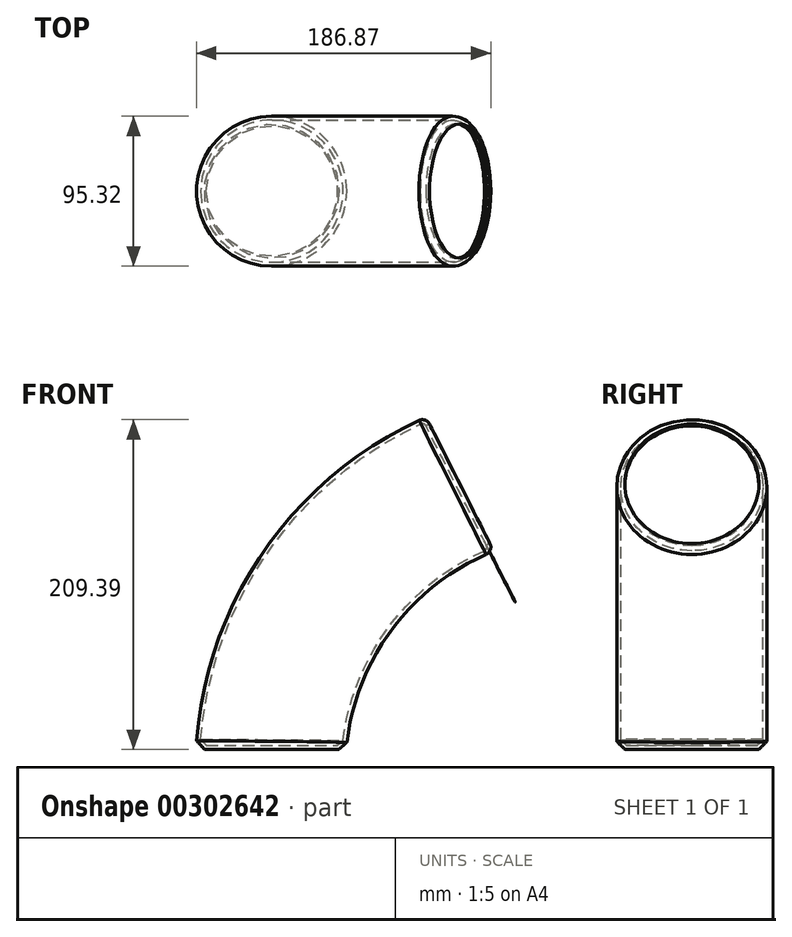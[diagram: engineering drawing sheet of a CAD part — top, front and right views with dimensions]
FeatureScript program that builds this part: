
annotation { "Feature Type Name" : "Feature", "Feature Type Description" : "" }
export const myFeature = defineFeature(function(context is Context, id is Id, definition is map)
    precondition{}
    {
        {
            var Q0;
            Q0=qCreatedBy(makeId("Top.planeOp"),FACE);
            var sketch = newSketch(context, id + "F0", { "sketchPlane" : qUnion([Q0])});
            skCircle(sketch, "E0", {"center": v(0, 0) * mm, "radius": 47.66 * mm});
            skSolve(sketch);
        }
        {
            var Q0;
            Q0=qCreatedBy(makeId("Front.planeOp"),FACE);
            var sketch = newSketch(context, id + "F1", { "sketchPlane" : qUnion([Q0])});
            skArc(sketch, "E1", {"start": v(119.97, 168.41) * mm, "mid": v(36.17, 101.17) * mm, "end": v(0, 0) * mm});
            skSolve(sketch);
        }
        {
            var Q0;
            Q0=makeQuery(id+"F0.imprint","IMPRINT",FACE,{"disambiguationData":[TD([[makeQuery(id+"F0.imprint","IMPRINT",EDGE,{"derivedFrom":sQuery(id+"F0.wireOp",EDGE,"E0")}),1.0]])]});
            var Q1;
            Q1=sQuery(id+"F1.wireOp",EDGE,"E1");
            sweep(context, id + "F2", {"profiles" : qUnion([Q0]), "path" : qUnion([Q1])});
        }
        {
            var Q0;
            Q0=makeQuery(id+"F2.opSweep","CAP_EDGE",EDGE,{"disambiguationData":[OSD([sQuery(id+"F0.wireOp",EDGE,"E0"),sQuery(id+"F1.wireOp",VERTEX,"E1.start")])],"isStart":false});
            fillet(context, id + "F3", {"entities" : qUnion([Q0]), "radius" : 5.08 * mm, "tangentPropagation" : true, "allowEdgeOverflow" : false});
        }
        {
            var Q0;
            Q0=makeQuery(id+"F2.opSweep","CAP_EDGE",EDGE,{"disambiguationData":[OSD([sQuery(id+"F0.wireOp",EDGE,"E0"),sQuery(id+"F1.wireOp",VERTEX,"E1.end")])],"isStart":true});
            chamfer(context, id + "F4", {"entities" : qUnion([Q0]), "width" : 5.08 * mm, "tangentPropagation" : true});
        }
        {
            var Q0;
            Q0=makeQuery(id+"F2.opSweep","CAP_FACE",FACE,{"disambiguationData":[OSD([sQuery(id+"F0.wireOp",EDGE,"E0"),sQuery(id+"F1.wireOp",VERTEX,"E1.start")])],"isStart":false});
            shell(context, id + "F5", {"entities" : qUnion([Q0]), "thickness" : 2.54 * mm});
        }
    });
